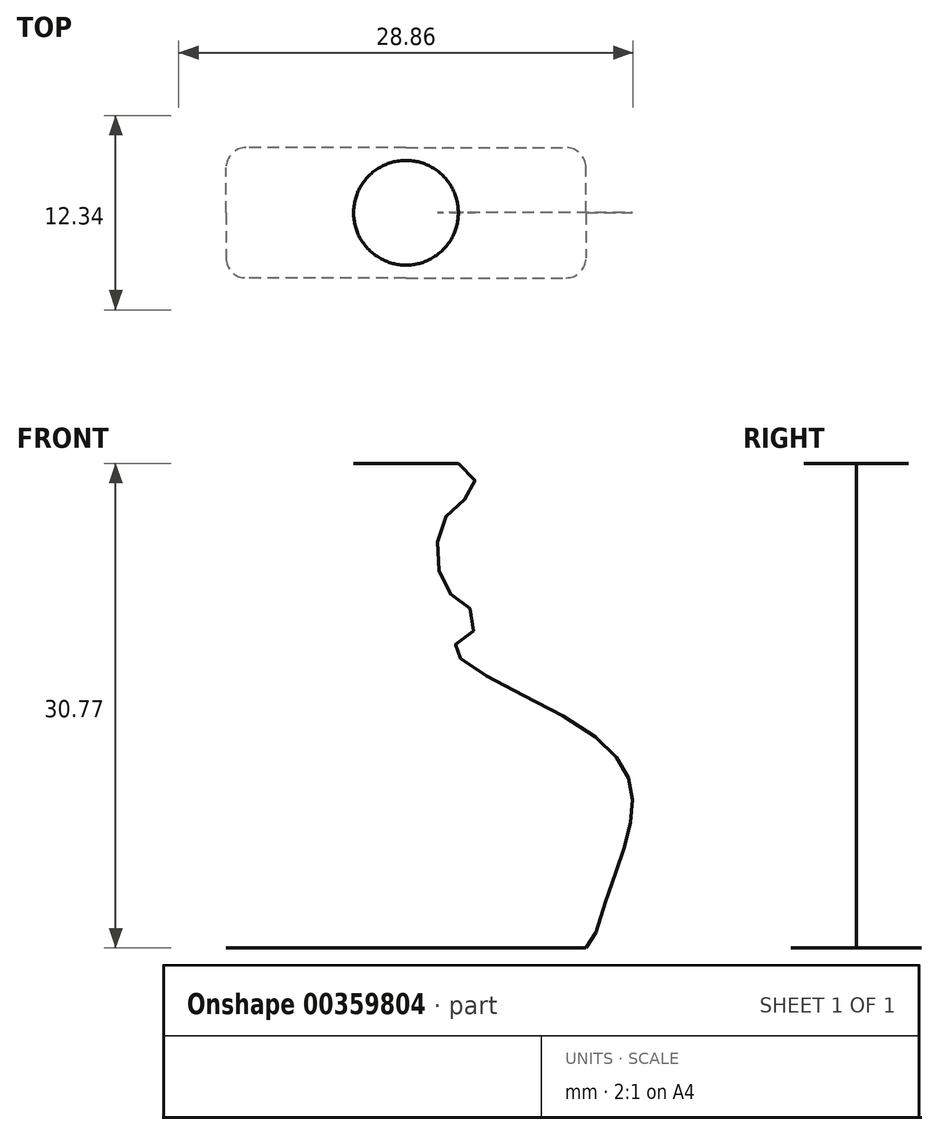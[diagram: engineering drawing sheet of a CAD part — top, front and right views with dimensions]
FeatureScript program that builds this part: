
annotation { "Feature Type Name" : "Feature", "Feature Type Description" : "" }
export const myFeature = defineFeature(function(context is Context, id is Id, definition is map)
    precondition{}
    {
        {
            var Q0;
            Q0=qCreatedBy(makeId("Front.planeOp"),FACE);
            var sketch = newSketch(context, id + "F0", { "sketchPlane" : qUnion([Q0])});
            skLineSegment(sketch, "E0", {"start": v(0, 0) * mm, "end": v(20.6, 0) * mm});
            skLineSegment(sketch, "E1", {"start": v(0, 0) * mm, "end": v(0, 30.77) * mm});
            skLineSegment(sketch, "E2", {"start": v(0, 30.77) * mm, "end": v(3.33, 30.77) * mm});
            skLineSegment(sketch, "E3", {"start": v(3.33, 30.77) * mm, "end": v(4.3, 29.93) * mm});
            skLineSegment(sketch, "E4", {"start": v(4.3, 29.93) * mm, "end": v(4.3, 28.96) * mm});
            skLineSegment(sketch, "E5", {"start": v(4.3, 28.96) * mm, "end": v(3.33, 28.26) * mm});
            skLineSegment(sketch, "E6", {"start": v(3.33, 28.26) * mm, "end": v(2.35, 28.26) * mm});
            skLineSegment(sketch, "E7", {"start": v(2.35, 28.26) * mm, "end": v(3.33, 22) * mm});
            skLineSegment(sketch, "E8", {"start": v(3.33, 22) * mm, "end": v(4.3, 21.3) * mm});
            skLineSegment(sketch, "E9", {"start": v(4.3, 21.3) * mm, "end": v(4.3, 20.15) * mm});
            skLineSegment(sketch, "E10", {"start": v(4.3, 20.15) * mm, "end": v(3.33, 19.44) * mm});
            skLineSegment(sketch, "E11", {"start": v(3.33, 19.44) * mm, "end": v(4.3, 15.57) * mm});
            skLineSegment(sketch, "E12", {"start": v(4.3, 15.57) * mm, "end": v(11.08, 14.07) * mm});
            skLineSegment(sketch, "E13", {"start": v(11.08, 14.07) * mm, "end": v(12.49, 2.34) * mm});
            skLineSegment(sketch, "E14", {"start": v(12.49, 2.34) * mm, "end": v(11.43, 0) * mm});
            skLineSegment(sketch, "E15", {"start": v(11.43, 0) * mm, "end": v(0, 0) * mm});
            skLineSegment(sketch, "E16", {"start": v(12.49, 2.34) * mm, "end": v(0, 2.34) * mm});
            skLineSegment(sketch, "E17", {"start": v(11.08, 14.07) * mm, "end": v(0, 14.07) * mm});
            skLineSegment(sketch, "E18", {"start": v(4.3, 15.57) * mm, "end": v(0, 15.57) * mm});
            skLineSegment(sketch, "E19", {"start": v(3.33, 19.44) * mm, "end": v(0, 19.44) * mm});
            skLineSegment(sketch, "E20", {"start": v(4.3, 20.15) * mm, "end": v(0, 20.15) * mm});
            skLineSegment(sketch, "E21", {"start": v(4.3, 21.3) * mm, "end": v(0, 21.3) * mm});
            skLineSegment(sketch, "E22", {"start": v(3.33, 22) * mm, "end": v(0, 22) * mm});
            skLineSegment(sketch, "E23", {"start": v(2.35, 28.26) * mm, "end": v(0, 28.26) * mm});
            skLineSegment(sketch, "E24", {"start": v(4.3, 28.96) * mm, "end": v(0, 28.96) * mm});
            skLineSegment(sketch, "E25", {"start": v(4.3, 29.93) * mm, "end": v(0, 29.93) * mm});
            skSolve(sketch);
        }
        {
            var Q0;
            Q0=qCreatedBy(makeId("Top.planeOp"),FACE);
            var Q1;
            Q1=sQuery(id+"F0.wireOp",VERTEX,"E13.end");
            cPlane(context, id + "F1", {"entities" : qUnion([Q0, Q1]), "cplaneType" : CPlaneType.PLANE_POINT, "offset" : 25.4 * mm, "width" : 152.4 * mm, "height" : 152.4 * mm});
        }
        {
            var Q0;
            Q0=qCreatedBy(id+"F1.planeOp",FACE);
            var Q1;
            Q1=sQuery(id+"F0.wireOp",VERTEX,"E12.end");
            cPlane(context, id + "F2", {"entities" : qUnion([Q0, Q1]), "cplaneType" : CPlaneType.PLANE_POINT, "offset" : 25.4 * mm, "width" : 152.4 * mm, "height" : 152.4 * mm});
        }
        {
            var Q0;
            Q0=qCreatedBy(id+"F2.planeOp",FACE);
            var Q1;
            Q1=sQuery(id+"F0.wireOp",VERTEX,"E11.end");
            cPlane(context, id + "F3", {"entities" : qUnion([Q0, Q1]), "cplaneType" : CPlaneType.PLANE_POINT, "offset" : 25.4 * mm, "width" : 152.4 * mm, "height" : 152.4 * mm});
        }
        {
            var Q0;
            Q0=qCreatedBy(id+"F3.planeOp",FACE);
            var Q1;
            Q1=sQuery(id+"F0.wireOp",VERTEX,"E11.start");
            cPlane(context, id + "F4", {"entities" : qUnion([Q0, Q1]), "cplaneType" : CPlaneType.PLANE_POINT, "offset" : 25.4 * mm, "width" : 152.4 * mm, "height" : 152.4 * mm});
        }
        {
            var Q0;
            Q0=sQuery(id+"F0.wireOp",VERTEX,"E10.start");
            var Q1;
            Q1=qCreatedBy(id+"F4.planeOp",FACE);
            cPlane(context, id + "F5", {"entities" : qUnion([Q0, Q1]), "cplaneType" : CPlaneType.PLANE_POINT, "offset" : 25.4 * mm, "width" : 152.4 * mm, "height" : 152.4 * mm});
        }
        {
            var Q0;
            Q0=sQuery(id+"F0.wireOp",VERTEX,"E9.start");
            var Q1;
            Q1=qCreatedBy(id+"F5.planeOp",FACE);
            cPlane(context, id + "F6", {"entities" : qUnion([Q0, Q1]), "cplaneType" : CPlaneType.PLANE_POINT, "offset" : 25.4 * mm, "width" : 152.4 * mm, "height" : 152.4 * mm});
        }
        {
            var Q0;
            Q0=qCreatedBy(id+"F6.planeOp",FACE);
            var Q1;
            Q1=sQuery(id+"F0.wireOp",VERTEX,"E8.start");
            cPlane(context, id + "F7", {"entities" : qUnion([Q0, Q1]), "cplaneType" : CPlaneType.PLANE_POINT, "offset" : 25.4 * mm, "width" : 152.4 * mm, "height" : 152.4 * mm});
        }
        {
            var Q0;
            Q0=qCreatedBy(id+"F7.planeOp",FACE);
            var Q1;
            Q1=sQuery(id+"F0.wireOp",VERTEX,"E6.start");
            cPlane(context, id + "F8", {"entities" : qUnion([Q0, Q1]), "cplaneType" : CPlaneType.PLANE_POINT, "offset" : 25.4 * mm, "width" : 152.4 * mm, "height" : 152.4 * mm});
        }
        {
            var Q0;
            Q0=sQuery(id+"F0.wireOp",VERTEX,"E5.start");
            var Q1;
            Q1=qCreatedBy(id+"F8.planeOp",FACE);
            cPlane(context, id + "F9", {"entities" : qUnion([Q0, Q1]), "cplaneType" : CPlaneType.PLANE_POINT, "offset" : 25.4 * mm, "width" : 152.4 * mm, "height" : 152.4 * mm});
        }
        {
            var Q0;
            Q0=qCreatedBy(id+"F9.planeOp",FACE);
            var Q1;
            Q1=sQuery(id+"F0.wireOp",VERTEX,"E4.start");
            cPlane(context, id + "F10", {"entities" : qUnion([Q0, Q1]), "cplaneType" : CPlaneType.PLANE_POINT, "offset" : 25.4 * mm, "width" : 152.4 * mm, "height" : 152.4 * mm});
        }
        {
            var Q0;
            Q0=qCreatedBy(id+"F10.planeOp",FACE);
            var Q1;
            Q1=sQuery(id+"F0.wireOp",VERTEX,"E3.start");
            cPlane(context, id + "F11", {"entities" : qUnion([Q0, Q1]), "cplaneType" : CPlaneType.PLANE_POINT, "offset" : 25.4 * mm, "width" : 152.4 * mm, "height" : 152.4 * mm});
        }
        {
            var Q0;
            Q0=qCreatedBy(makeId("Top.planeOp"),FACE);
            var sketch = newSketch(context, id + "F12", { "sketchPlane" : qUnion([Q0])});
            skLineSegment(sketch, "E26", {"start": v(0, 0) * mm, "end": v(11.43, 0) * mm, "construction": true});
            skLineSegment(sketch, "E27.top", {"start": v(0, 4.14) * mm, "end": v(10.16, 4.14) * mm});
            skLineSegment(sketch, "E27.left", {"start": v(0, 0) * mm, "end": v(0, 4.14) * mm, "construction": true});
            skLineSegment(sketch, "E27.right", {"start": v(11.43, 0) * mm, "end": v(11.43, 2.87) * mm});
            skLineSegment(sketch, "E28.MirrorCS", {"start": v(0, -4.14) * mm, "end": v(10.16, -4.14) * mm});
            skLineSegment(sketch, "E29.MirrorCS", {"start": v(11.43, 0) * mm, "end": v(11.43, -2.87) * mm});
            skLineSegment(sketch, "E30.MirrorCS", {"start": v(0, 4.14) * mm, "end": v(-10.16, 4.14) * mm});
            skLineSegment(sketch, "E31.MirrorCS", {"start": v(-11.43, 0) * mm, "end": v(-11.43, 2.87) * mm});
            skLineSegment(sketch, "E32.MirrorCS", {"start": v(-11.43, 0) * mm, "end": v(-11.43, -2.87) * mm});
            skLineSegment(sketch, "E33.MirrorCS", {"start": v(0, -4.14) * mm, "end": v(-10.16, -4.14) * mm});
            skPoint(sketch, "E34.visualSharp", {"position": v(-11.43, 4.14) * mm});
            skArc(sketch, "E34.filletArc", {"start": v(-10.16, 4.14) * mm, "mid": v(-11.06, 3.76) * mm, "end": v(-11.43, 2.87) * mm});
            skArc(sketch, "E35.MirrorCS", {"start": v(10.16, 4.14) * mm, "mid": v(11.06, 3.76) * mm, "end": v(11.43, 2.87) * mm});
            skArc(sketch, "E36.MirrorCS", {"start": v(-10.16, -4.14) * mm, "mid": v(-11.06, -3.76) * mm, "end": v(-11.43, -2.87) * mm});
            skArc(sketch, "E37.MirrorCS", {"start": v(10.16, -4.14) * mm, "mid": v(11.06, -3.76) * mm, "end": v(11.43, -2.87) * mm});
            skPoint(sketch, "E38.orphan", {"position": v(11.43, 4.14) * mm});
            skPoint(sketch, "E39.orphan", {"position": v(11.43, -4.14) * mm});
            skPoint(sketch, "E40.orphan", {"position": v(-11.43, -4.14) * mm});
            skSolve(sketch);
        }
        {
            var Q0;
            Q0=qCreatedBy(id+"F1.planeOp",FACE);
            var sketch = newSketch(context, id + "F13", { "sketchPlane" : qUnion([Q0])});
            skLineSegment(sketch, "E41", {"start": v(0, 0) * mm, "end": v(12.49, 0) * mm, "construction": true});
            skLineSegment(sketch, "E42", {"start": v(12.49, 0) * mm, "end": v(12.49, 3.7) * mm});
            skLineSegment(sketch, "E43", {"start": v(10.97, 5.22) * mm, "end": v(0, 5.22) * mm});
            skLineSegment(sketch, "E44", {"start": v(0, 5.22) * mm, "end": v(0, 0) * mm, "construction": true});
            skPoint(sketch, "E45.visualSharp", {"position": v(12.49, 5.22) * mm});
            skArc(sketch, "E45.filletArc", {"start": v(12.49, 3.7) * mm, "mid": v(12.04, 4.78) * mm, "end": v(10.97, 5.22) * mm});
            skLineSegment(sketch, "E46.MirrorCS", {"start": v(-10.97, 5.22) * mm, "end": v(0, 5.22) * mm});
            skArc(sketch, "E47.MirrorCS", {"start": v(-12.49, 3.7) * mm, "mid": v(-12.04, 4.78) * mm, "end": v(-10.97, 5.22) * mm});
            skLineSegment(sketch, "E48.MirrorCS", {"start": v(-12.49, 0) * mm, "end": v(-12.49, 3.7) * mm});
            skLineSegment(sketch, "E49.MirrorCS", {"start": v(12.49, 0) * mm, "end": v(12.49, -3.7) * mm});
            skArc(sketch, "E50.MirrorCS", {"start": v(12.49, -3.7) * mm, "mid": v(12.04, -4.78) * mm, "end": v(10.97, -5.22) * mm});
            skLineSegment(sketch, "E51.MirrorCS", {"start": v(10.97, -5.22) * mm, "end": v(0, -5.22) * mm});
            skLineSegment(sketch, "E52.MirrorCS", {"start": v(-10.97, -5.22) * mm, "end": v(0, -5.22) * mm});
            skArc(sketch, "E53.MirrorCS", {"start": v(-12.49, -3.7) * mm, "mid": v(-12.04, -4.78) * mm, "end": v(-10.97, -5.22) * mm});
            skLineSegment(sketch, "E54.MirrorCS", {"start": v(-12.49, 0) * mm, "end": v(-12.49, -3.7) * mm});
            skSolve(sketch);
        }
        {
            var Q0;
            Q0=qCreatedBy(id+"F2.planeOp",FACE);
            var sketch = newSketch(context, id + "F14", { "sketchPlane" : qUnion([Q0])});
            skLineSegment(sketch, "E55", {"start": v(0, 0) * mm, "end": v(11.08, 0) * mm, "construction": true});
            skLineSegment(sketch, "E56", {"start": v(11.08, 0) * mm, "end": v(11.08, 3.7) * mm});
            skLineSegment(sketch, "E57", {"start": v(10.24, 4.55) * mm, "end": v(0, 4.55) * mm});
            skLineSegment(sketch, "E58", {"start": v(0, 4.55) * mm, "end": v(0, 0) * mm, "construction": true});
            skPoint(sketch, "E59.visualSharp", {"position": v(11.08, 4.55) * mm});
            skArc(sketch, "E59.filletArc", {"start": v(11.08, 3.7) * mm, "mid": v(10.83, 4.3) * mm, "end": v(10.24, 4.55) * mm});
            skLineSegment(sketch, "E60.MirrorCS", {"start": v(10.24, -4.55) * mm, "end": v(0, -4.55) * mm});
            skArc(sketch, "E61.MirrorCS", {"start": v(11.08, -3.7) * mm, "mid": v(10.83, -4.3) * mm, "end": v(10.24, -4.55) * mm});
            skLineSegment(sketch, "E62.MirrorCS", {"start": v(11.08, 0) * mm, "end": v(11.08, -3.7) * mm});
            skLineSegment(sketch, "E63.MirrorCS", {"start": v(-10.24, 4.55) * mm, "end": v(0, 4.55) * mm});
            skArc(sketch, "E64.MirrorCS", {"start": v(-11.08, 3.7) * mm, "mid": v(-10.83, 4.3) * mm, "end": v(-10.24, 4.55) * mm});
            skLineSegment(sketch, "E65.MirrorCS", {"start": v(-11.08, 0) * mm, "end": v(-11.08, 3.7) * mm});
            skLineSegment(sketch, "E66.MirrorCS", {"start": v(-11.08, 0) * mm, "end": v(-11.08, -3.7) * mm});
            skArc(sketch, "E67.MirrorCS", {"start": v(-11.08, -3.7) * mm, "mid": v(-10.83, -4.3) * mm, "end": v(-10.24, -4.55) * mm});
            skLineSegment(sketch, "E68.MirrorCS", {"start": v(-10.24, -4.55) * mm, "end": v(0, -4.55) * mm});
            skSolve(sketch);
        }
        {
            var Q0;
            Q0=qCreatedBy(id+"F4.planeOp",FACE);
            var sketch = newSketch(context, id + "F15", { "sketchPlane" : qUnion([Q0])});
            skLineSegment(sketch, "E69", {"start": v(0, 0) * mm, "end": v(3.33, 0) * mm});
            skCircle(sketch, "E70", {"center": v(0, 0) * mm, "radius": 3.33 * mm});
            skSolve(sketch);
        }
        {
            var Q0;
            Q0=qCreatedBy(id+"F5.planeOp",FACE);
            var sketch = newSketch(context, id + "F16", { "sketchPlane" : qUnion([Q0])});
            skLineSegment(sketch, "E71", {"start": v(0, 0) * mm, "end": v(4.3, 0) * mm});
            skCircle(sketch, "E72", {"center": v(0, 0) * mm, "radius": 4.3 * mm});
            skSolve(sketch);
        }
        {
            var Q0;
            Q0=qCreatedBy(id+"F6.planeOp",FACE);
            var sketch = newSketch(context, id + "F17", { "sketchPlane" : qUnion([Q0])});
            skLineSegment(sketch, "E73", {"start": v(0, 0) * mm, "end": v(4.3, 0) * mm});
            skCircle(sketch, "E74", {"center": v(0, 0) * mm, "radius": 4.3 * mm});
            skSolve(sketch);
        }
        {
            var Q0;
            Q0=qCreatedBy(id+"F7.planeOp",FACE);
            var sketch = newSketch(context, id + "F18", { "sketchPlane" : qUnion([Q0])});
            skLineSegment(sketch, "E75", {"start": v(0, 0) * mm, "end": v(3.33, 0) * mm});
            skCircle(sketch, "E76", {"center": v(0, 0) * mm, "radius": 3.33 * mm});
            skSolve(sketch);
        }
        {
            var Q0;
            Q0=qCreatedBy(id+"F8.planeOp",FACE);
            var sketch = newSketch(context, id + "F19", { "sketchPlane" : qUnion([Q0])});
            skLineSegment(sketch, "E77", {"start": v(0, 0) * mm, "end": v(2.35, 0) * mm});
            skLineSegment(sketch, "E78", {"start": v(2.35, 0) * mm, "end": v(3.33, 0) * mm});
            skCircle(sketch, "E79", {"center": v(0, 0) * mm, "radius": 3.33 * mm});
            skSolve(sketch);
        }
        {
            var Q0;
            Q0=qCreatedBy(id+"F9.planeOp",FACE);
            var sketch = newSketch(context, id + "F20", { "sketchPlane" : qUnion([Q0])});
            skLineSegment(sketch, "E80", {"start": v(0, 0) * mm, "end": v(4.3, 0) * mm});
            skCircle(sketch, "E81", {"center": v(0, 0) * mm, "radius": 4.3 * mm});
            skSolve(sketch);
        }
        {
            var Q0;
            Q0=qCreatedBy(id+"F10.planeOp",FACE);
            var sketch = newSketch(context, id + "F21", { "sketchPlane" : qUnion([Q0])});
            skLineSegment(sketch, "E82", {"start": v(0, 0) * mm, "end": v(4.3, 0) * mm});
            skCircle(sketch, "E83", {"center": v(0, 0) * mm, "radius": 4.3 * mm});
            skSolve(sketch);
        }
        {
            var Q0;
            Q0=qCreatedBy(id+"F11.planeOp",FACE);
            var sketch = newSketch(context, id + "F22", { "sketchPlane" : qUnion([Q0])});
            skLineSegment(sketch, "E84", {"start": v(0, 0) * mm, "end": v(3.33, 0) * mm});
            skCircle(sketch, "E85", {"center": v(0, 0) * mm, "radius": 3.33 * mm});
            skSolve(sketch);
        }
        {
            var Q0;
            Q0=makeQuery(id+"F12.imprint","IMPRINT",FACE,{"disambiguationData":[TD([[makeQuery(id+"F12.imprint","IMPRINT",EDGE,{"derivedFrom":sQuery(id+"F12.wireOp",EDGE,"E27.top")}),-1.0]])]});
            var Q1;
            Q1=makeQuery(id+"F13.imprint","IMPRINT",FACE,{"disambiguationData":[TD([[makeQuery(id+"F13.imprint","IMPRINT",EDGE,{"derivedFrom":sQuery(id+"F13.wireOp",EDGE,"E42")}),1.0]])]});
            var Q2;
            Q2=makeQuery(id+"F14.imprint","IMPRINT",FACE,{"disambiguationData":[TD([[makeQuery(id+"F14.imprint","IMPRINT",EDGE,{"derivedFrom":sQuery(id+"F14.wireOp",EDGE,"E56")}),1.0]])]});
            var Q3;
            Q3=makeQuery(id+"F15.imprint","IMPRINT",FACE,{"disambiguationData":[TD([[makeQuery(id+"F15.imprint","IMPRINT",EDGE,{"derivedFrom":sQuery(id+"F15.wireOp",EDGE,"E70")}),1.0]])]});
            var Q4;
            Q4=makeQuery(id+"F16.imprint","IMPRINT",FACE,{"disambiguationData":[TD([[makeQuery(id+"F16.imprint","IMPRINT",EDGE,{"derivedFrom":sQuery(id+"F16.wireOp",EDGE,"E72")}),1.0]])]});
            var Q5;
            Q5=makeQuery(id+"F17.imprint","IMPRINT",FACE,{"disambiguationData":[TD([[makeQuery(id+"F17.imprint","IMPRINT",EDGE,{"derivedFrom":sQuery(id+"F17.wireOp",EDGE,"E74")}),1.0]])]});
            var Q6;
            Q6=makeQuery(id+"F18.imprint","IMPRINT",FACE,{"disambiguationData":[TD([[makeQuery(id+"F18.imprint","IMPRINT",EDGE,{"derivedFrom":sQuery(id+"F18.wireOp",EDGE,"E76")}),1.0]])]});
            var Q7;
            Q7=makeQuery(id+"F19.imprint","IMPRINT",FACE,{"disambiguationData":[TD([[makeQuery(id+"F19.imprint","IMPRINT",EDGE,{"derivedFrom":sQuery(id+"F19.wireOp",EDGE,"E79")}),1.0]])]});
            var Q8;
            Q8=makeQuery(id+"F20.imprint","IMPRINT",FACE,{"disambiguationData":[TD([[makeQuery(id+"F20.imprint","IMPRINT",EDGE,{"derivedFrom":sQuery(id+"F20.wireOp",EDGE,"E81")}),1.0]])]});
            var Q9;
            Q9=makeQuery(id+"F21.imprint","IMPRINT",FACE,{"disambiguationData":[TD([[makeQuery(id+"F21.imprint","IMPRINT",EDGE,{"derivedFrom":sQuery(id+"F21.wireOp",EDGE,"E83")}),1.0]])]});
            var Q10;
            Q10=makeQuery(id+"F22.imprint","IMPRINT",FACE,{"disambiguationData":[TD([[makeQuery(id+"F22.imprint","IMPRINT",EDGE,{"derivedFrom":sQuery(id+"F22.wireOp",EDGE,"E85")}),1.0]])]});
            var Q11;
            Q11=sQuery(id+"F14.wireOp",VERTEX,"E56.start");
            var Q12;
            Q12=sQuery(id+"F15.wireOp",VERTEX,"E69.end");
            var Q13;
            Q13=sQuery(id+"F16.wireOp",VERTEX,"E71.end");
            var Q14;
            Q14=sQuery(id+"F17.wireOp",VERTEX,"E73.end");
            var Q15;
            Q15=sQuery(id+"F18.wireOp",VERTEX,"E75.end");
            var Q16;
            Q16=sQuery(id+"F19.wireOp",VERTEX,"E78.end");
            var Q17;
            Q17=sQuery(id+"F20.wireOp",VERTEX,"E80.end");
            var Q18;
            Q18=sQuery(id+"F21.wireOp",VERTEX,"E82.end");
            var Q19;
            Q19=sQuery(id+"F22.wireOp",VERTEX,"E84.end");
            var Q20;
            Q20=sQuery(id+"F13.wireOp",VERTEX,"E49.MirrorCS.start");
            var Q21;
            Q21=sQuery(id+"F12.wireOp",VERTEX,"E29.MirrorCS.start");
            loft(context, id + "F23", {"startCondition" : LoftEndDerivativeType.TANGENT_TO_PROFILE, "startMagnitude" : 1.2, "endCondition" : LoftEndDerivativeType.TANGENT_TO_PROFILE, "endMagnitude" : 0.6, "sheetProfilesArray" : [{ "sheetProfileEntities" : qUnion([Q0]) }, { "sheetProfileEntities" : qUnion([Q1]) }, { "sheetProfileEntities" : qUnion([Q2]) }, { "sheetProfileEntities" : qUnion([Q3]) }, { "sheetProfileEntities" : qUnion([Q4]) }, { "sheetProfileEntities" : qUnion([Q5]) }, { "sheetProfileEntities" : qUnion([Q6]) }, { "sheetProfileEntities" : qUnion([Q7]) }, { "sheetProfileEntities" : qUnion([Q8]) }, { "sheetProfileEntities" : qUnion([Q9]) }, { "sheetProfileEntities" : qUnion([Q10]) }], "matchConnections" : true, "connections" : [{ "connectionEntities" : qUnion([Q11, Q12, Q13, Q14, Q15, Q16, Q17, Q18, Q19, Q20, Q21]), "connectionEdgeQueries" : qUnion([]), "connectionEdgeParameters" : [] }]});
        }
    });
